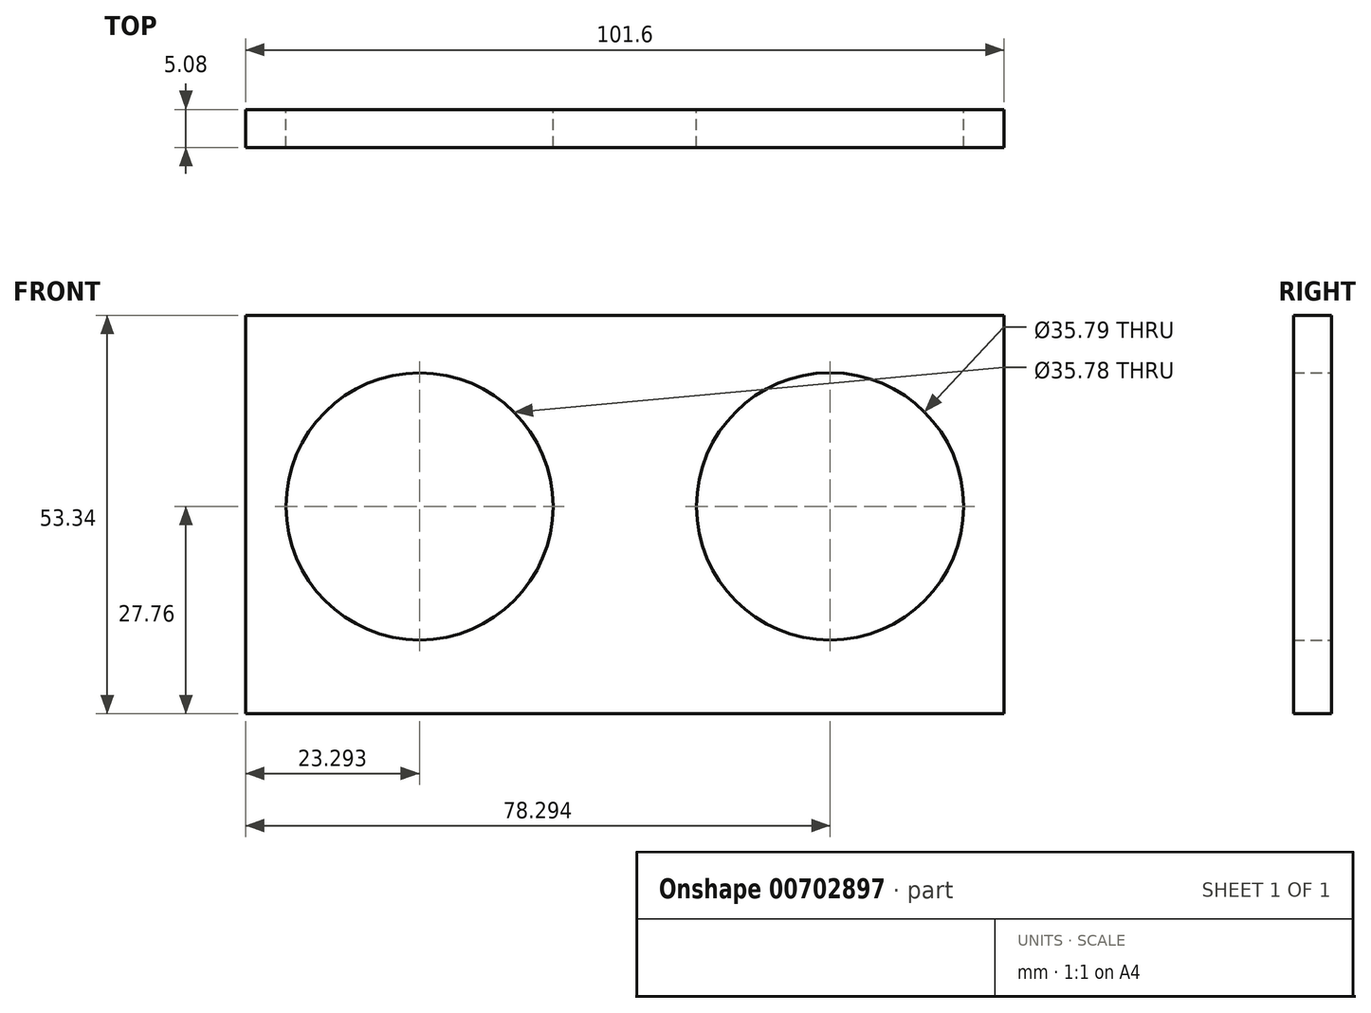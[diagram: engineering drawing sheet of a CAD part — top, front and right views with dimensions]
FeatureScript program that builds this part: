
annotation { "Feature Type Name" : "Feature", "Feature Type Description" : "" }
export const myFeature = defineFeature(function(context is Context, id is Id, definition is map)
    precondition{}
    {
        {
            var Q0;
            Q0=qCreatedBy(makeId("Front.planeOp"),FACE);
            var sketch = newSketch(context, id + "F0", { "sketchPlane" : qUnion([Q0])});
            skLineSegment(sketch, "E0", {"start": v(-44.81, 25.58) * mm, "end": v(-44.81, -27.76) * mm});
            skLineSegment(sketch, "E1", {"start": v(-44.81, -27.76) * mm, "end": v(56.79, -27.76) * mm});
            skLineSegment(sketch, "E2", {"start": v(56.79, -27.76) * mm, "end": v(56.79, 25.58) * mm});
            skLineSegment(sketch, "E3", {"start": v(56.79, 25.58) * mm, "end": v(-44.81, 25.58) * mm});
            skCircle(sketch, "E4", {"center": v(33.48, 0) * mm, "radius": 17.9 * mm});
            skCircle(sketch, "E5", {"center": v(-21.52, 0) * mm, "radius": 17.89 * mm});
            skSolve(sketch);
        }
        {
            var Q0;
            Q0 = qSketchRegion(id + "F0", true);
            extrude(context, id + "F1", {"entities" : qUnion([Q0]), "depth" : 5.08 * mm, "offsetDistance" : 25.4 * mm});
        }
    });
